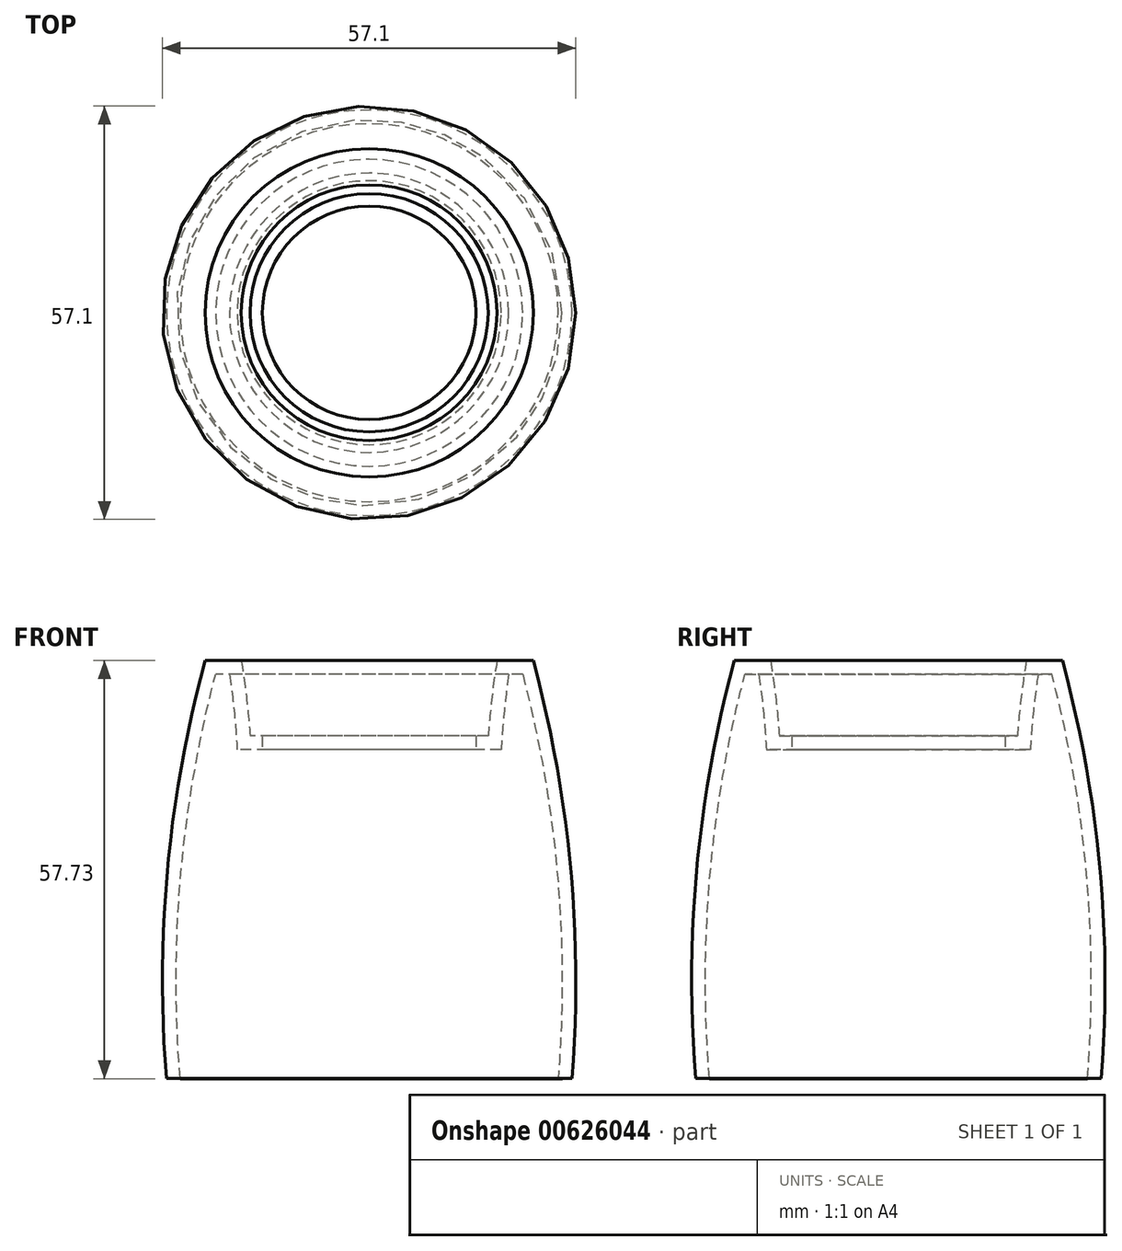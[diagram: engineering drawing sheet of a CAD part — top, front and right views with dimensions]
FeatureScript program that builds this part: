
annotation { "Feature Type Name" : "Feature", "Feature Type Description" : "" }
export const myFeature = defineFeature(function(context is Context, id is Id, definition is map)
    precondition{}
    {
        {
            var Q0;
            Q0=qCreatedBy(makeId("Front.planeOp"),FACE);
            var sketch = newSketch(context, id + "F0", { "sketchPlane" : qUnion([Q0])});
            skLineSegment(sketch, "E0", {"start": v(-4.54, 35.47) * mm, "end": v(-6.45, 35.47) * mm});
            skArc(sketch, "E1", {"start": v(-6.45, 35.47) * mm, "mid": v(-11.26, 7.76) * mm, "end": v(-11.35, -20.36) * mm});
            skArc(sketch, "E2", {"start": v(-3.48, 25.07) * mm, "mid": v(-3.89, 30.28) * mm, "end": v(-4.54, 35.47) * mm});
            skLineSegment(sketch, "E3", {"start": v(-3.48, 25.07) * mm, "end": v(0, 25.07) * mm});
            skArc(sketch, "E4.0", {"start": v(-7.91, 37.37) * mm, "mid": v(-13.08, 8.75) * mm, "end": v(-13.26, -20.33) * mm});
            skLineSegment(sketch, "E4.1", {"start": v(-2.91, 37.37) * mm, "end": v(-7.91, 37.37) * mm});
            skArc(sketch, "E4.2", {"start": v(-1.7, 26.97) * mm, "mid": v(-2.18, 32.18) * mm, "end": v(-2.91, 37.37) * mm});
            skLineSegment(sketch, "E4.3", {"start": v(-1.7, 26.97) * mm, "end": v(0, 26.97) * mm});
            skLineSegment(sketch, "E5", {"start": v(0, 26.97) * mm, "end": v(0, 25.07) * mm});
            skLineSegment(sketch, "E6", {"start": v(-13.26, -20.33) * mm, "end": v(-11.35, -20.36) * mm});
            skLineSegment(sketch, "E7", {"start": v(0, 26.02) * mm, "end": v(14.75, 26) * mm});
            skLineSegment(sketch, "E8", {"start": v(14.75, 26) * mm, "end": v(14.75, 24.77) * mm});
            skSolve(sketch);
        }
        {
            var Q0;
            Q0 = qSketchRegion(id + "F0", true);
            var Q1;
            Q1=sQuery(id+"F0.wireOp",EDGE,"E8");
            revolve(context, id + "F1", {"surfaceOperationType" : NewSurfaceOperationType.NEW, "entities" : qUnion([Q0]), "axis" : qUnion([Q1]), "revolveType" : RevolveType.FULL});
        }
    });
